# Revit family: PRD_FrankeWS_WlHngWshBsns_ANIMA_ANMX450
name_source: partatom
category: Plumbing Fixtures
revit_build: Autodesk Revit 2018 (Build: 20190510_1515(x64)
units: mm (PartAtom-declared; Revit-internal decimal feet)

## family parameters
Cut with Voids When Loaded = No
Host = Face
OmniClass Number = 23.45.05.14.14
OmniClass Title = Sinks/Lavatories
Part Type = Normal
Room Calculation Point = No
Round Connector Dimension = Use Diameter
Shared = No

## types (1)
- ANMX450
    AssetType = Fixed
    BIMObjectName = PRD_AR_WallHungWashBasins_AnimaWashBasin_ANMX450
    Category = Pr_40_20_96_96, Wall-hung wash basins
    Color = Stainless steel
    Default Elevation = 850 mm  [stored 2.78871 ft]
    Description = Wash basin for wall mounting, stainless steel, surface satin finished, material thickness 1.2 mm, seamless welded bowl with dimension 360 x 272 x 135 mm, made of one piece, for high risk vandalism areas due to seamless closed trap cover and semicircular shape, rounded edges, bowl with revolving channel, 40 mm tap ledge, without overflow, 1 1/2" flat perforated waste, drainage centric, incl. trap DN 32, with pressed soap dish, inclusive mounting plate conform to EN 31, inclusive stainless steel screws and dowels.
    DrainSize = 32  [stored 0.104987 ft]
    DurationUnit = year
    Features = Wash basin, stainless steel, 1.20 mm, satin finished, wall mounting, 450x280x400 mm (WxHxD)
    Finish = Satin finished
    Form = Wall hung wash basin
    GrossWeight = 7.12 kg
    IfcExportAs = IfcSanitaryTerminalType
    IfcExportType = WASHHANDBASIN
    IntegralAccessories = Stainless steel screws and dowels
    Manufacturer = KWC Group AG
    ManufacturerName = KWC Group AG
    ManufacturerURL = www.kwc.com
    Material = Stainless steel
    MaterialsBody = Stainless steel
    MaterialsFinishAndColour = Stainless steel
    Model = ANMX450
    ModelNumber = 2000071857
    ModelReference = ANMX450
    NBSDescription = Wall hung wash basins
    NBSReference = 45-35-70/369
    Name = ANIMA Wash basins ANMX450
    NetWeight = 6.20 kg
    NominalDepth = 280 mm  [stored 0.918635 ft]
    NominalHeight = 280 mm  [stored 0.918635 ft]
    NominalLength = 400 mm  [stored 1.31234 ft]
    NominalWidth = 450 mm  [stored 1.47638 ft]
    ProductInformation = https://pim.kwc.com
    Size = 450 x 280 x 400 mm
    URL = www.kwc.com
    Uniclass2015Code = Pr_40_20_96_96
    Uniclass2015Title = Wall-hung wash basins
    Uniclass2015Version = Products v1.7
    Version = 1
    WarrantyDurationUnit = year
    WashHandBasinMounting = WallHung
    WashHandBasinType = HandRinse
    WashbasinMaterial = PRD_AR_StainlessSteel_SatinFinished
    WasteSize = 32  [stored 0.104987 ft]
    WaterSupplyOverflowAndWasteHolesOverflow = None
    WaterSupplyOverflowAndWasteHolesWaste = CENTER-BACK
    WaterSupplyOverflowAndWasteHolesWaterSupply = No tapholes

note: [stored X ft] marks values corroborated as IEEE doubles in the binary element streams (Revit-internal decimal feet)

## geometry (parser evidence)
native form markers: Sweep x2
no freeform markers — native parametric forms only
